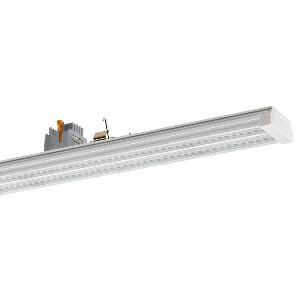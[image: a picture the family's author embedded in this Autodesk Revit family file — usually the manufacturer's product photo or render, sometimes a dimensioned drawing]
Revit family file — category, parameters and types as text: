
# Revit family: conveo_-_cvg_15000_840_w-l_da_7_226848299-00804968_43c9
name_source: partatom
category: Lighting Fixtures
units: mm (PartAtom-declared; Revit-internal decimal feet)

## family parameters
Cut with Voids When Loaded = No
Host = Face
Light Source = No
Part Type = Normal
Room Calculation Point = No
Round Connector Dimension = Use Diameter
Shared = No

## types (1)
- CONVEO - CVG 15000/840/W-L/DA/7 (1 x LED, 14800 lm, 4000K)
    Apparent Load = 86 VA
    Approval mark = CE
    CIE Flux Codes = 85 97 99 100 100
    Color Rendering = 80-89
    Color Temperature = 4000K
    Control Gear = Electronic ballast
    Default Elevation = 1800 mm
    Description = CVG 15000/840/W-L/DA/7|Continuous-row system|light source: LED|work equipment: Adjustable electronic ballast, digital DALI|connected load: 220-240 V, 50-60 Hz|Power consumption: approx. 86 W|luminous flux: 14800 lm|luminous efficacy: 172 lm/W|colour temperature: Cold white, ca. 4000 K|color rendering index (CRI): >= 80|chromaticity tolerance:  3 SDCM|System of protection: IP 54|class of protection: I|technology: Continuously dimmable|luminaire body|material: Aluminium|surface: Powder coatet|colour: White|lamp cover: Acrylic (PMMA), Satine|weight (net): approx. 2.2 kg|Fastening: Available separately|maximum ambient temperature: 41 ░C|glare control: Lens optics|Approval mark: VDE - ENEC|
    Frequency = 50 Hz
    Height = 70 mm
    Lamp = 1 x LED
    Lamp Light Flux = 14800 lm
    Lamp count = 1
    Length = 1500 mm
    Luminous efficacy = 172 lm/W
    Manufacturer = Waldmann
    ModVariant = No
    Model = 226848299-00804968
    Mounting Place = Ceiling
    Mounting Type = Pendant
    Number of Poles = 1
    OnlyDefault = Yes
    Power Factor = 1
    Product Name = CONVEO - CVG 15000/840/W-L/DA/7
    Product group = Continuous-row system (industry)
    ProductGroupID = 301
    Protection Class = Protection class I
    Protection Degree = IP 54
    RLX_Detail_Level = 1
    RlxData = <blob elided: 135973 chars, md5=0c2e4814>
    Socket = socket
    Standby Power = 0 W
    System Light Flux = 14800 lm
    System Power = 86 W
    Type Comments = Product without accessories
    Type Image = 226848299-00804968_2l7.jpg
    URL = http://relux.com
    VarID = ---
    Voltage = 230 V
    Voltage Range = 220-240 V
    Weight = 0.00 kg
    Width = 64 mm

## geometry (parser evidence)
native form markers: Blend x4, Sweep x10
no freeform markers — native parametric forms only
